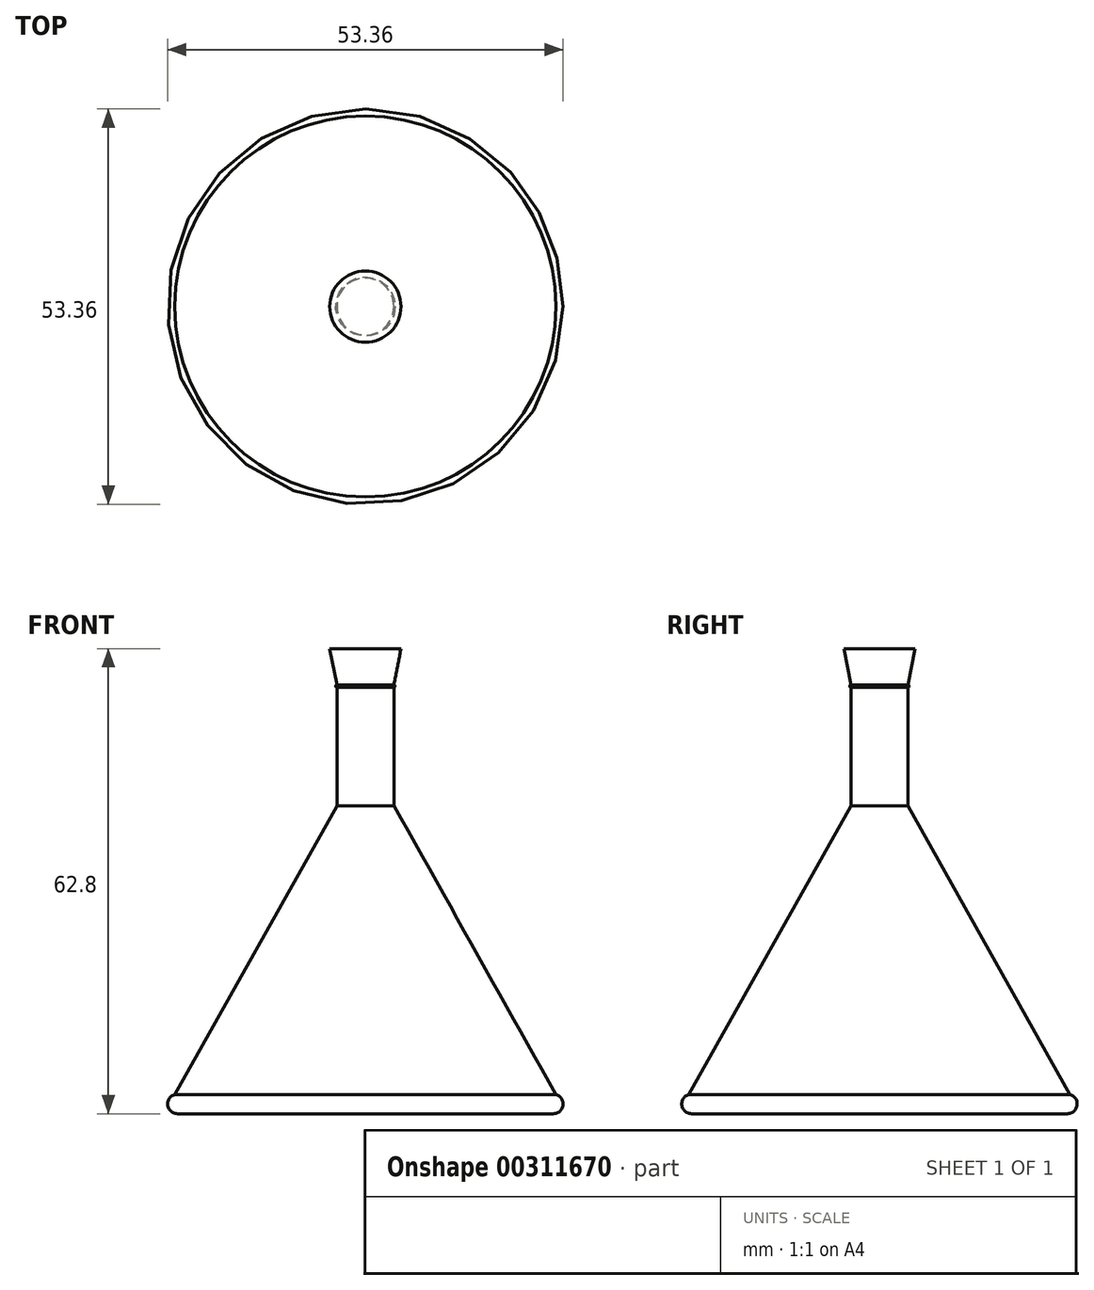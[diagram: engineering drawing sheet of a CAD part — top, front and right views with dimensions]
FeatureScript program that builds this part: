
annotation { "Feature Type Name" : "Feature", "Feature Type Description" : "" }
export const myFeature = defineFeature(function(context is Context, id is Id, definition is map)
    precondition{}
    {
        {
            var Q0;
            Q0=qCreatedBy(makeId("Front.planeOp"),FACE);
            var sketch = newSketch(context, id + "F0", { "sketchPlane" : qUnion([Q0])});
            skLineSegment(sketch, "E0", {"start": v(0, 32.1) * mm, "end": v(0, -30.7) * mm});
            skLineSegment(sketch, "E1", {"start": v(0, -30.7) * mm, "end": v(-25.35, -30.7) * mm});
            skArc(sketch, "E2", {"start": v(-25.72, -28.1) * mm, "mid": v(-26.67, -29.56) * mm, "end": v(-25.35, -30.7) * mm});
            skLineSegment(sketch, "E3", {"start": v(-25.72, -28.1) * mm, "end": v(-3.85, 10.87) * mm});
            skLineSegment(sketch, "E4", {"start": v(-3.85, 10.87) * mm, "end": v(-3.85, 26.84) * mm});
            skArc(sketch, "E5", {"start": v(-3.85, 27.21) * mm, "mid": v(-4, 27.03) * mm, "end": v(-3.85, 26.84) * mm});
            skLineSegment(sketch, "E6", {"start": v(-3.85, 27.21) * mm, "end": v(-4.8, 32.1) * mm});
            skLineSegment(sketch, "E7", {"start": v(-4.8, 32.1) * mm, "end": v(0, 32.1) * mm});
            skSolve(sketch);
        }
        {
            var Q0;
            Q0 = qSketchRegion(id + "F0", true);
            var Q1;
            Q1=sQuery(id+"F0.wireOp",EDGE,"E0");
            revolve(context, id + "F1", {"entities" : qUnion([Q0]), "axis" : qUnion([Q1]), "revolveType" : RevolveType.FULL});
        }
    });
